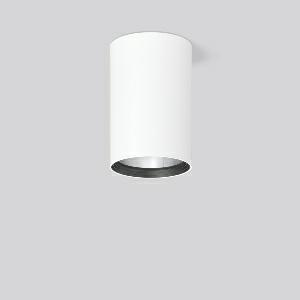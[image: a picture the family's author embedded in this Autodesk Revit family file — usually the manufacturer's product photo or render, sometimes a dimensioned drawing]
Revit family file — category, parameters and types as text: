
# Revit family: heledon_maxi_a_931224_002_1_76_c384
name_source: partatom
category: Lighting Fixtures
units: mm (PartAtom-declared; Revit-internal decimal feet)

## family parameters
Cut with Voids When Loaded = No
Host = Face
Light Source = No
Part Type = Normal
Room Calculation Point = No
Round Connector Dimension = Use Diameter
Shared = No

## types (1)
- HELEDON maxi A (1 x LED Modul 940, 4550 lm, 4000)
    Apparent Load = 35 VA
    Approval mark = CE
    CIE Flux Codes = 100 100 100 100 100
    Color Rendering = 92
    Color Temperature = 4000
    Default Elevation = 1800 mm
    Description = Series: HELEDON maxi
Cylindrical surface-mounted downlight. Housing: die-cast aluminium, powder-coated. Internal ceiling frame polycarbonate with bayonet mounting. Black plastic ring and recessed LED to prevent glare from the side. Optical assembly with reflector made of MIRO-Silver with 98% total light reflection for outstanding efficiency - can be changed without tools. Best colour rendering index Ra>90. Suitable for Ceiling mounting. Easy installation with a separate ceiling frame with bayonet mounting and plug connection. Driver integrated. Connected via plug-in connector. High quality converter without flickering and stroboscopic effect. The following accessories can be mounted without use of tools: interchangeable lenses, decorative glasses, honeycomb louvre, clear and frosted diffusers, white interchangeable plastic ring. 
Colour: traffic white, matt (RAL 9016)
Diameter: 123 mm
Height: 183 mm
Lamp: LED
Socket: without socket
Colour temperature: 4000K
Colour rendering index (CRI): 92
System power: 35 W
Rated luminous flux: 4550 lm
Luminous efficiency: 130 lm/W
Control gear: Converter, dimmable, DALI
Protection class: I
Type of protection: IP 20
    Height = 183 mm
    Lamp = 1 x LED Modul 940
    Lamp Light Flux = 4550 lm
    Lamp count = 1
    Length = 123 mm
    Lifetime = 50000 h
    Luminous efficacy = 130 lm/W
    Manufacturer = RZB
    ModVariant = No
    Model = 931224.002.1.76
    Mounting Place = Ceiling
    Mounting Type = Surface mounted
    Number of Poles = 1
    OnlyDefault = Yes
    Power Factor = 1
    Product Name = HELEDON maxi A
    Product group = Surface mounted downlights
    ProductGroupID = 302
    Protection Class = Protection class I
    Protection Degree = IP 20
    RLX_Detail_Level = 1
    RLX_Emergency_Light_Flux = 0 lm
    RLX_Emergency_Type = 0
    RLX_Emergency_Type_DB = No
    RlxData = <blob elided: 98705 chars, md5=a9782453>
    Socket = socket
    Standby Power = 0 W
    System Light Flux = 4550 lm
    System Power = 35 W
    Type Comments = Product without accessories
    Type Image = 931192.002.jpg
    URL = http://relux.com
    VarID = ---
    Voltage = 230 V
    Voltage Range = 220-240 V
    Weight = 0.00 kg
    Width = 0 mm  [stored 0 ft]

note: [stored X ft] marks values corroborated as IEEE doubles in the binary element streams (Revit-internal decimal feet)

## geometry (parser evidence)
native form markers: Blend x4, Sweep x10
no freeform markers — native parametric forms only
